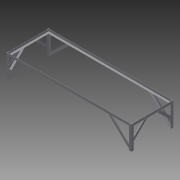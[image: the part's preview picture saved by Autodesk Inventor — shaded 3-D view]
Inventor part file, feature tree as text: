
AUTODESK INVENTOR PART (.ipt)
format: ipt  version: 2014 (Build 180170000, 170)  size: 219,136 bytes
history: native  units: in
note: dims shown in document units (in); Inventor stores cm internally (conversion verified against a paired STEP export)
features: extrude x7, sketch x4, mirror x2, projected_geometry x1
ambient origin geometry x8: Origin, YZ Plane, XZ Plane, XY Plane, X Axis, Y Axis, Z Axis, Center Point
bodies: Solid1 (feature_tree)
feature tree (14):
  sketch  "Sketch1"  dims[d0=79.0in d1=26.25in]
  extrude  "Extrusion1"  Depth=26.25in
  extrude  "Extrusion2"  Depth=76.25in
  extrude  "Extrusion3"  Depth=0.125in
  sketch  "Sketch4"  dims[d4=0.125in d5=0.125in]
  extrude  "Extrusion5"  Depth=1.375in TaperAngle=0.0deg
  extrude  "Extrusion6"  Depth=0.125in
  sketch  "Sketch5"  dims[d6=0.125in d7=0.0in d8=1.375in d9=0.0in d10=0.125in d15=0.125in d17=15.0in d18=0.0in d23=1.5in d24=12.0in d25=5.0in d28=0.125in d29=1.375in d30=0.0in d31=0.125in d32=0.0in d33=1.5in d34=1.0in d35=0.125in d36=18.0in d37=0.125in d38=0.0in d39=1.5in d40=0.0in d41=1.5in d42=1.5in]
  extrude  "Extrusion7"  Depth=0.125in
  extrude  "Extrusion8"  Depth=15.0in TaperAngle=0.0deg
  mirror  "Mirror1"
  mirror  "Mirror2"
  sketch  "Sketch2"  dims[d2=23.5in d3=76.25in]
  projected_geometry  "Projected Loop1"
